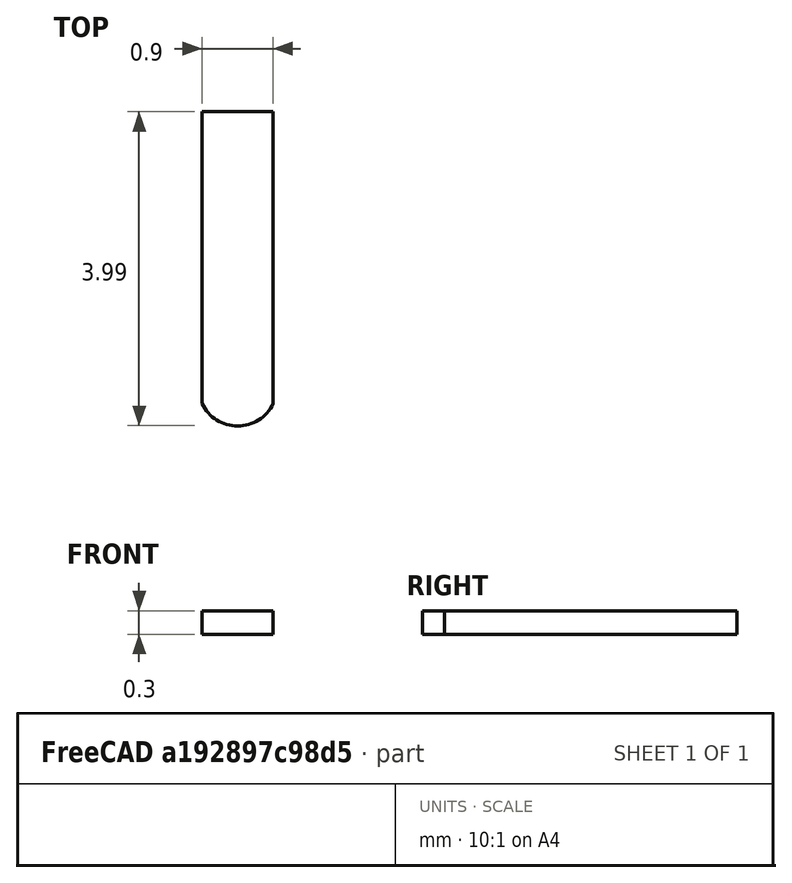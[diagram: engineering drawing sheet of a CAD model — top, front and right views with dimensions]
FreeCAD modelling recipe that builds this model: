
FCSTD DOCUMENT  (FreeCAD 0.19R16699 (Git))
Label: RD901F_Terminal_Type_20
License: All rights reserved
LicenseURL: http://en.wikipedia.org/wiki/All_rights_reserved
objects: Sketcher::SketchObject×1, PartDesign::Pad×1, PartDesign::Body×1, App::Part×1
note: 4 computed .brp shape members not serialized (recipe doc carries the construction recipe); baked Part::Feature solids carry a one-line shape summary decoded from their .brp

FEATURE [Sketcher::SketchObject] Sketch
  MapMode = 5
  Support = -> [XY_Plane]
  sketch-geometry (7):
    g0: ArcOfCircle CenterX=0 CenterY=-3.49746 CenterZ=0 NormalX=0 NormalY=0 NormalZ=1 AngleXU=0 Radius=0.497458 StartAngle=3.58195 EndAngle=5.84283
    g1: LineSegment StartX=-0.45 StartY=-3.70951 StartZ=0 EndX=-0.45 EndY=0 EndZ=0
    g2: LineSegment StartX=0.45 StartY=-3.70951 StartZ=0 EndX=0.45 EndY=0 EndZ=0
    g3: LineSegment StartX=-0.45 StartY=0 StartZ=0 EndX=0.45 EndY=0 EndZ=0
    g4: LineSegment [constr] StartX=0.45 StartY=-3.70951 StartZ=0 EndX=-0.45 EndY=-3.70951 EndZ=0
    g5: GeomPoint X=0 Y=-3 Z=0
    g6: LineSegment [constr] StartX=0 StartY=-3 StartZ=0 EndX=0 EndY=-3.49746 EndZ=0
  constraints (18):
    c: PointOnObject(g0,g-2)
    c: Coincident(g1,g0)
    c: PointOnObject(g1,g-1)
    c: Vertical(g1)
    c: Coincident(g2,g0)
    c: PointOnObject(g2,g-1)
    c: Vertical(g2)
    c: Coincident(g3,g1)
    c: Coincident(g3,g2)
    c: Coincident(g4,g0)
    c: Coincident(g4,g0)
    c: Horizontal(g4)
    c: DistanceX(g3,g3) = 0.9
    c: PointOnObject(g5,g0)
    c: Coincident(g6,g5)
    c: Coincident(g6,g0)
    c: PointOnObject(g5,g-2)
    c: DistanceY(g5,g-1) = 3
FEATURE [PartDesign::Pad] Pad
  Length = 0.3
  Length2 = 100
  Midplane = true
  Profile = -> Sketch
  Type = 0
FEATURE [PartDesign::Body] Body  label="RD901F_Terminal_Type_20_1"
  Group = -> [Sketch,Pad]
  Origin = -> Origin
  Tip = -> Pad
FEATURE [App::Part] Part  label="RD901F_Terminal_Type_20"
  Group = -> [Body]
  Origin = -> Origin001
